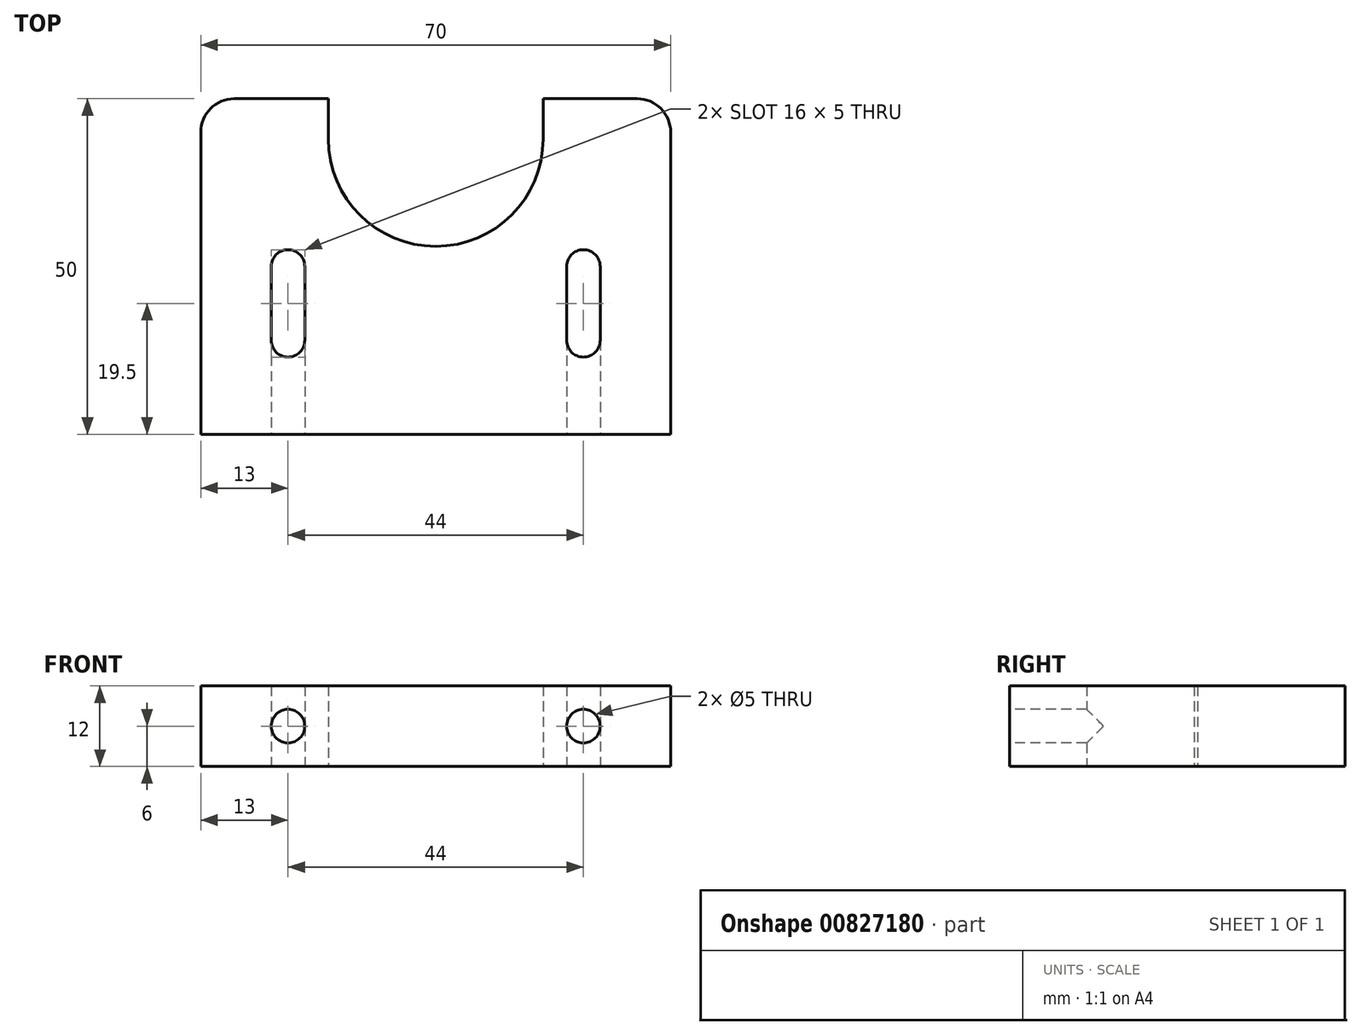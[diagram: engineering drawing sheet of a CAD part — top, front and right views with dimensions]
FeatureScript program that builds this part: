
annotation { "Feature Type Name" : "Feature", "Feature Type Description" : "" }
export const myFeature = defineFeature(function(context is Context, id is Id, definition is map)
    precondition{}
    {
        {
            var Q0;
            Q0=qCreatedBy(makeId("Top.planeOp"),FACE);
            var sketch = newSketch(context, id + "F0", { "sketchPlane" : qUnion([Q0])});
            skLineSegment(sketch, "E0.bottom", {"start": v(5.25, 143.35) * mm, "end": v(11.25, 143.35) * mm, "construction": true});
            skLineSegment(sketch, "E1", {"start": v(35, -17) * mm, "end": v(35, 44) * mm, "construction": true});
            skCircle(sketch, "E2", {"center": v(35, 44) * mm, "radius": 12.5 * mm, "construction": true});
            skCircle(sketch, "E3", {"center": v(35, 44) * mm, "radius": 28 * mm, "construction": true});
            skLineSegment(sketch, "E4", {"start": v(35, 0) * mm, "end": v(70, 0) * mm});
            skLineSegment(sketch, "E5", {"start": v(70, 0) * mm, "end": v(70, 50) * mm});
            skLineSegment(sketch, "E6", {"start": v(70, 50) * mm, "end": v(51, 50) * mm});
            skLineSegment(sketch, "E7", {"start": v(0, 50) * mm, "end": v(0, 0) * mm});
            skLineSegment(sketch, "E8", {"start": v(0, 0) * mm, "end": v(35, 0) * mm});
            skLineSegment(sketch, "E9", {"start": v(51, 44) * mm, "end": v(51, 50) * mm});
            skLineSegment(sketch, "E10", {"start": v(19, 44) * mm, "end": v(19, 50) * mm});
            skArc(sketch, "E11.trimOffspring", {"start": v(19, 44) * mm, "mid": v(35, 28) * mm, "end": v(51, 44) * mm});
            skLineSegment(sketch, "E12.trimOffspring", {"start": v(19, 50) * mm, "end": v(0, 50) * mm});
            skLineSegment(sketch, "E13", {"start": v(7, 44) * mm, "end": v(7, 0) * mm, "construction": true});
            skLineSegment(sketch, "E14", {"start": v(63, 44) * mm, "end": v(63, 0) * mm, "construction": true});
            skLineSegment(sketch, "E15", {"start": v(35, 44) * mm, "end": v(51, 44) * mm, "construction": true});
            skLineSegment(sketch, "E16", {"start": v(35, 44) * mm, "end": v(19, 44) * mm, "construction": true});
            skLineSegment(sketch, "E17", {"start": v(35, 44) * mm, "end": v(35, 14) * mm, "construction": true});
            skLineSegment(sketch, "E18", {"start": v(35, 14) * mm, "end": v(57, 14) * mm, "construction": true});
            skLineSegment(sketch, "E19", {"start": v(35, 14) * mm, "end": v(13, 14) * mm, "construction": true});
            skLineSegment(sketch, "E20", {"start": v(57, 14) * mm, "end": v(57, 19.5) * mm, "construction": true});
            skCircle(sketch, "E21", {"center": v(13, 19.5) * mm, "radius": 2.5 * mm, "construction": true});
            skCircle(sketch, "E22", {"center": v(57, 19.5) * mm, "radius": 2.5 * mm, "construction": true});
            skLineSegment(sketch, "E23", {"start": v(13, 25) * mm, "end": v(15.5, 25) * mm, "construction": true});
            skLineSegment(sketch, "E24", {"start": v(15.5, 25) * mm, "end": v(10.5, 25) * mm, "construction": true});
            skLineSegment(sketch, "E25", {"start": v(13, 14) * mm, "end": v(10.5, 14) * mm, "construction": true});
            skLineSegment(sketch, "E26", {"start": v(57, 19.5) * mm, "end": v(57, -25.1) * mm, "construction": true});
            skLineSegment(sketch, "E27", {"start": v(13, 19.5) * mm, "end": v(13, -40.75) * mm, "construction": true});
            skLineSegment(sketch, "E28", {"start": v(57, 0) * mm, "end": v(57, 10) * mm, "construction": true});
            skLineSegment(sketch, "E29", {"start": v(13, 0) * mm, "end": v(13, 10) * mm, "construction": true});
            skPoint(sketch, "E30.middle", {"position": v(57, 10) * mm});
            skPoint(sketch, "E31.middle", {"position": v(13, 10) * mm});
            skLineSegment(sketch, "E32", {"start": v(13, 14) * mm, "end": v(13, 25) * mm});
            skLineSegment(sketch, "E33", {"start": v(57, 14) * mm, "end": v(57, 25) * mm});
            skArc(sketch, "E34.0.startCap", {"start": v(15.5, 14) * mm, "mid": v(13, 11.5) * mm, "end": v(10.5, 14) * mm});
            skArc(sketch, "E34.0.endCap", {"start": v(10.5, 25) * mm, "mid": v(13, 27.5) * mm, "end": v(15.5, 25) * mm});
            skLineSegment(sketch, "E34.0.left", {"start": v(10.5, 14) * mm, "end": v(10.5, 25) * mm});
            skLineSegment(sketch, "E34.0.right", {"start": v(15.5, 14) * mm, "end": v(15.5, 25) * mm});
            skArc(sketch, "E34.1.startCap", {"start": v(59.5, 14) * mm, "mid": v(57, 11.5) * mm, "end": v(54.5, 14) * mm});
            skArc(sketch, "E34.1.endCap", {"start": v(54.5, 25) * mm, "mid": v(57, 27.5) * mm, "end": v(59.5, 25) * mm});
            skLineSegment(sketch, "E34.1.left", {"start": v(54.5, 14) * mm, "end": v(54.5, 25) * mm});
            skLineSegment(sketch, "E34.1.right", {"start": v(59.5, 14) * mm, "end": v(59.5, 25) * mm});
            skSolve(sketch);
        }
        {
            var Q0;
            Q0=makeQuery(id+"F0.imprint","IMPRINT",FACE,{"disambiguationData":[TD([[makeQuery(id+"F0.imprint","IMPRINT",EDGE,{"derivedFrom":sQuery(id+"F0.wireOp",EDGE,"E4")}),1.0]])]});
            extrude(context, id + "F1", {"entities" : qUnion([Q0]), "depth" : 12 * mm, "offsetDistance" : 25 * mm});
        }
        {
            var Q0;
            Q0=makeQuery(id+"F1.opExtrude","SWEPT_FACE",FACE,{"disambiguationData":[OSD([sQuery(id+"F0.wireOp",EDGE,"E4"),sQuery(id+"F0.wireOp",EDGE,"E8")])]});
            var sketch = newSketch(context, id + "F2", { "sketchPlane" : qUnion([Q0])});
            skLineSegment(sketch, "E35", {"start": v(0, 12) * mm, "end": v(13, 12) * mm, "construction": true});
            skLineSegment(sketch, "E36", {"start": v(13, 12) * mm, "end": v(13, 6) * mm, "construction": true});
            skLineSegment(sketch, "E37", {"start": v(70, 12) * mm, "end": v(57, 12) * mm, "construction": true});
            skLineSegment(sketch, "E38", {"start": v(57, 12) * mm, "end": v(57, 6) * mm, "construction": true});
            skLineSegment(sketch, "E39", {"start": v(13, 12) * mm, "end": v(35, 12) * mm, "construction": true});
            skLineSegment(sketch, "E40", {"start": v(35, 12) * mm, "end": v(57, 12) * mm, "construction": true});
            skCircle(sketch, "E41", {"center": v(13, 6) * mm, "radius": 2.5 * mm});
            skCircle(sketch, "E42", {"center": v(57, 6) * mm, "radius": 2.5 * mm});
            skSolve(sketch);
        }
        {
            var Q0;
            Q0=qSketchRegion(id+"F2",true);
            extrude(context, id + "F3", {"entities" : qUnion([Q0]), "operationType" : NewBodyOperationType.REMOVE, "oppositeDirection" : true, "depth" : 15 * mm, "offsetDistance" : 25 * mm});
        }
        {
            var Q0;
            Q0=makeQuery(id+"F1.opExtrude","SWEPT_EDGE",EDGE,{"disambiguationData":[OSD([sQuery(id+"F0.wireOp",EDGE,"E5"),sQuery(id+"F0.wireOp",EDGE,"E6")])]});
            var Q1;
            Q1=makeQuery(id+"F1.opExtrude","SWEPT_EDGE",EDGE,{"disambiguationData":[OSD([sQuery(id+"F0.wireOp",EDGE,"E7"),sQuery(id+"F0.wireOp",EDGE,"E12.trimOffspring")])]});
            fillet(context, id + "F4", {"entities" : qUnion([Q0, Q1]), "radius" : 5 * mm, "tangentPropagation" : true, "allowEdgeOverflow" : false});
        }
    });
